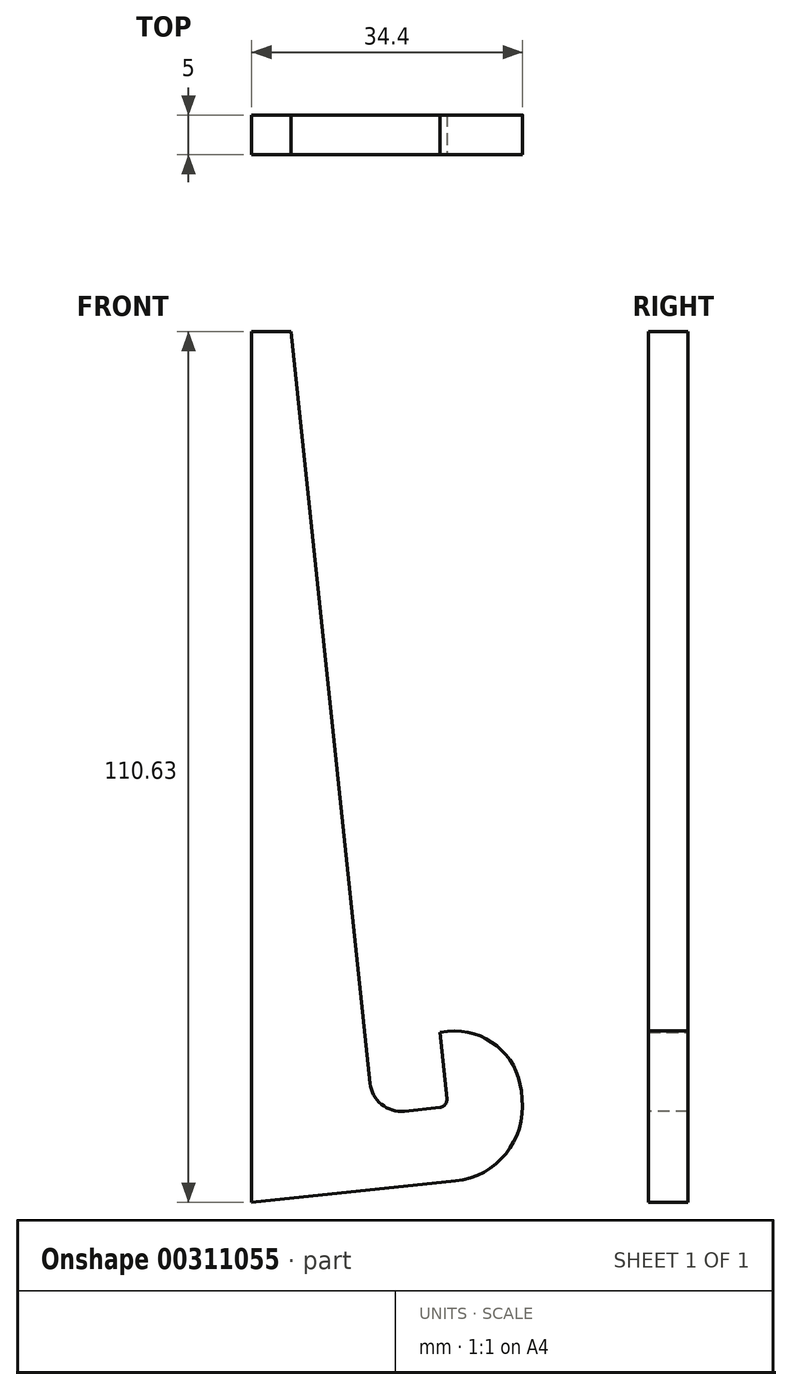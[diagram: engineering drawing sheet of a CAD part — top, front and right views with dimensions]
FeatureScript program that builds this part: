
annotation { "Feature Type Name" : "Feature", "Feature Type Description" : "" }
export const myFeature = defineFeature(function(context is Context, id is Id, definition is map)
    precondition{}
    {
        {
            var Q0;
            Q0=qCreatedBy(makeId("Front.planeOp"),FACE);
            var sketch = newSketch(context, id + "F0", { "sketchPlane" : qUnion([Q0])});
            skLineSegment(sketch, "E0", {"start": v(0, 110.63) * mm, "end": v(0, 0) * mm});
            skLineSegment(sketch, "E1", {"start": v(0, 110.63) * mm, "end": v(5, 110.63) * mm});
            skLineSegment(sketch, "E2", {"start": v(5, 110.63) * mm, "end": v(15.45, 11.18) * mm});
            skLineSegment(sketch, "E3", {"start": v(15.45, 11.18) * mm, "end": v(24.9, 12.17) * mm});
            skLineSegment(sketch, "E4", {"start": v(24.9, 12.17) * mm, "end": v(23.9, 21.62) * mm});
            skLineSegment(sketch, "E5", {"start": v(23.9, 21.62) * mm, "end": v(33.36, 22.61) * mm});
            skLineSegment(sketch, "E6", {"start": v(33.36, 22.61) * mm, "end": v(35.34, 3.71) * mm});
            skLineSegment(sketch, "E7", {"start": v(35.34, 3.71) * mm, "end": v(0, 0) * mm});
            skSolve(sketch);
        }
        {
            var Q0;
            Q0 = qSketchRegion(id + "F0", true);
            extrude(context, id + "F1", {"entities" : qUnion([Q0]), "depth" : 5 * mm});
        }
        {
            var Q0;
            Q0=makeQuery(id+"F1.opExtrude","SWEPT_EDGE",EDGE,{"disambiguationData":[OSD([sQuery(id+"F0.wireOp",EDGE,"E5"),sQuery(id+"F0.wireOp",EDGE,"E6")])]});
            fillet(context, id + "F2", {"entities" : qUnion([Q0]), "radius" : 8.5 * mm, "tangentPropagation" : true, "allowEdgeOverflow" : false});
        }
        {
            var Q0;
            Q0=makeQuery(id+"F1.opExtrude","SWEPT_EDGE",EDGE,{"disambiguationData":[OSD([sQuery(id+"F0.wireOp",EDGE,"E2"),sQuery(id+"F0.wireOp",EDGE,"E3")])]});
            fillet(context, id + "F3", {"entities" : qUnion([Q0]), "radius" : 4 * mm, "tangentPropagation" : true, "allowEdgeOverflow" : false});
        }
        {
            var Q0;
            Q0=makeQuery(id+"F1.opExtrude","SWEPT_EDGE",EDGE,{"disambiguationData":[OSD([sQuery(id+"F0.wireOp",EDGE,"E6"),sQuery(id+"F0.wireOp",EDGE,"E7")])]});
            fillet(context, id + "F4", {"entities" : qUnion([Q0]), "radius" : 9.5 * mm, "tangentPropagation" : true, "allowEdgeOverflow" : false});
        }
        {
            var Q0;
            Q0=makeQuery(id+"F1.opExtrude","SWEPT_EDGE",EDGE,{"disambiguationData":[OSD([sQuery(id+"F0.wireOp",EDGE,"E3"),sQuery(id+"F0.wireOp",EDGE,"E4")])]});
            fillet(context, id + "F5", {"entities" : qUnion([Q0]), "radius" : 1 * mm, "tangentPropagation" : true, "allowEdgeOverflow" : false});
        }
    });
